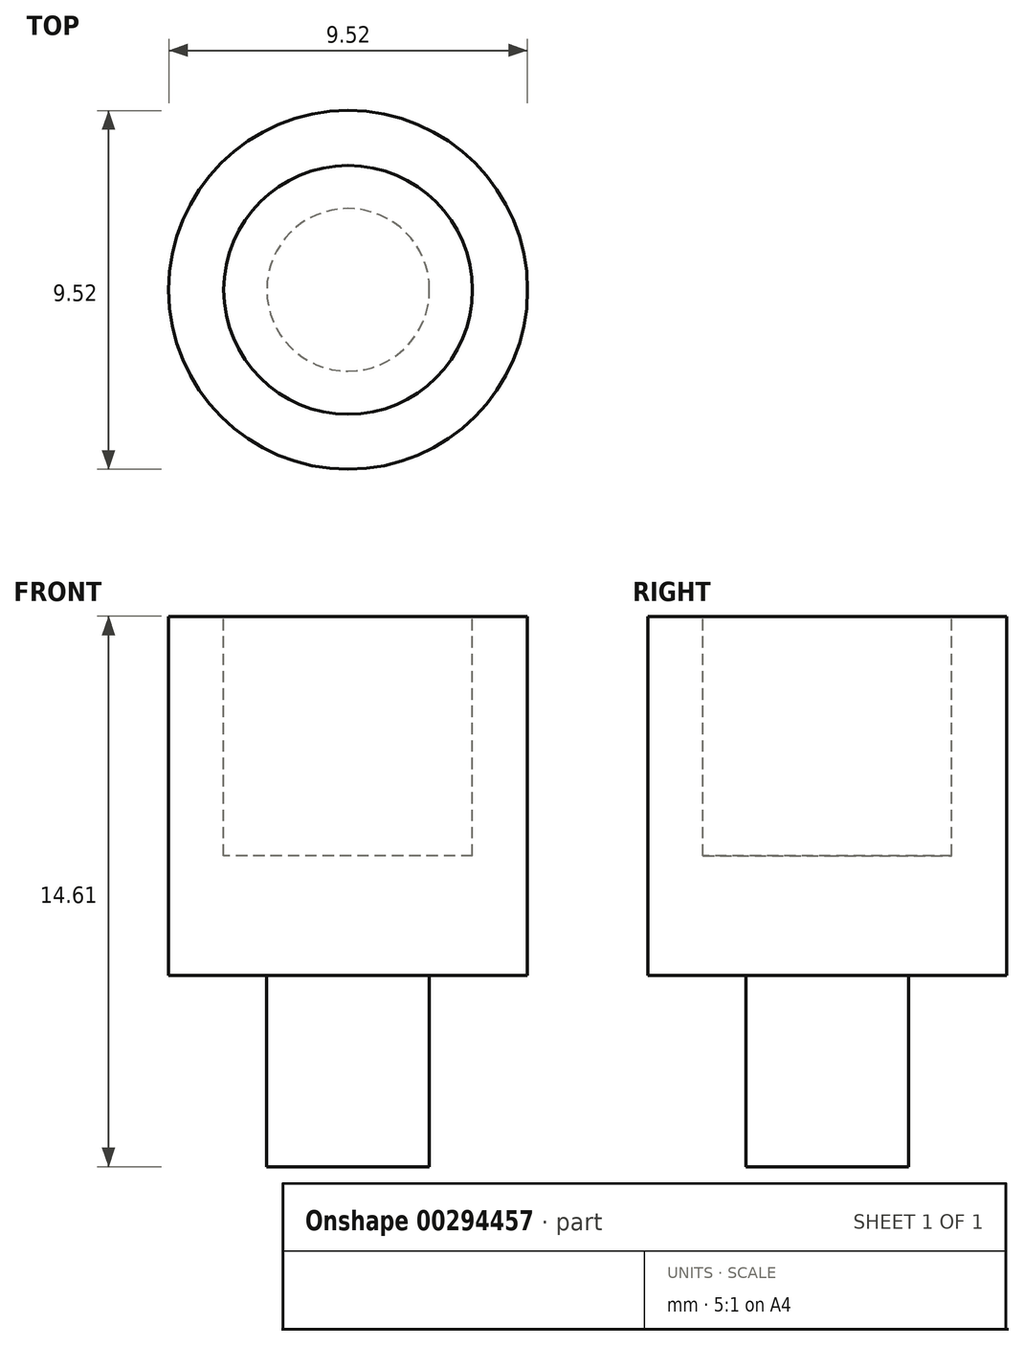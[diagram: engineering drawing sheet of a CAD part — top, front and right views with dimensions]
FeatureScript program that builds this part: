
annotation { "Feature Type Name" : "Feature", "Feature Type Description" : "" }
export const myFeature = defineFeature(function(context is Context, id is Id, definition is map)
    precondition{}
    {
        {
            var Q0;
            Q0=qCreatedBy(makeId("Top.planeOp"),FACE);
            var sketch = newSketch(context, id + "F0", { "sketchPlane" : qUnion([Q0])});
            skCircle(sketch, "E0", {"center": v(0, 0) * mm, "radius": 2.16 * mm});
            skCircle(sketch, "E1", {"center": v(0, 0) * mm, "radius": 4.76 * mm});
            skSolve(sketch);
        }
        {
            var Q0;
            Q0 = qSketchRegion(id + "F0", true);
            var Q1;
            Q1=makeQuery(id+"F0.imprint","IMPRINT",FACE,{"disambiguationData":[TD([[makeQuery(id+"F0.imprint","IMPRINT",EDGE,{"derivedFrom":sQuery(id+"F0.wireOp",EDGE,"E0")}),1.0]])]});
            extrude(context, id + "F1", {"entities" : qUnion([Q0, Q1]), "depth" : 9.52 * mm});
        }
        {
            var Q0;
            Q0=makeQuery(id+"F0.imprint","IMPRINT",FACE,{"disambiguationData":[TD([[makeQuery(id+"F0.imprint","IMPRINT",EDGE,{"derivedFrom":sQuery(id+"F0.wireOp",EDGE,"E0")}),1.0]])]});
            extrude(context, id + "F2", {"entities" : qUnion([Q0]), "operationType" : NewBodyOperationType.ADD, "oppositeDirection" : true, "depth" : 5.08 * mm});
        }
        {
            var Q0;
            Q0=makeQuery(id+"F1.opExtrude","CAP_FACE",FACE,{"disambiguationData":[OSD([sQuery(id+"F0.wireOp",EDGE,"E1")])],"isStart":false});
            var sketch = newSketch(context, id + "F3", { "sketchPlane" : qUnion([Q0])});
            skCircle(sketch, "E2", {"center": v(0, 0) * mm, "radius": 3.3 * mm});
            skSolve(sketch);
        }
        {
            var Q0;
            Q0 = qSketchRegion(id + "F3", true);
            extrude(context, id + "F4", {"entities" : qUnion([Q0]), "operationType" : NewBodyOperationType.REMOVE, "oppositeDirection" : true, "depth" : 6.35 * mm});
        }
    });
